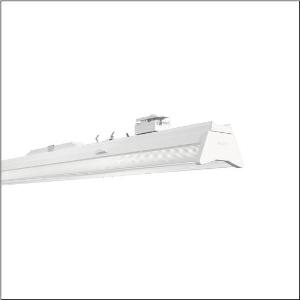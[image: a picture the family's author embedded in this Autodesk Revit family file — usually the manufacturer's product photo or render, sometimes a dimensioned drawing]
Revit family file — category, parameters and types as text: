
# Revit family: licross_r__21_performance_mo_52tm167n485g_c234
name_source: partatom
category: Lighting Fixtures
units: mm (PartAtom-declared; Revit-internal decimal feet)

## family parameters
Cut with Voids When Loaded = No
Host = Face
Light Source = No
Part Type = Normal
Room Calculation Point = No
Round Connector Dimension = Use Diameter
Shared = No

## types (1)
- Licross® 21 Performance MO (1 x LED, 8720 lm, 47.9 W, 4000K)
    Apparent Load = 48 VA
    CIE Flux Codes = 66 88 96 79 100
    Color Rendering = 80
    Color Temperature = 4000K
    Default Elevation = 1800 mm
    Description = Licross® 21 Performance MO, luminaire insert, of sheet steel, galvanised, coil coated, white, length: 1.500mm, width: 120mm, height: 123mm, LED rated luminous flux: 8.720lm, light colour: 840, SDCM (Standard Deviation of Colour Matching)MacAdam ≤ 3 SDCM (initial), control gear: ON/OFF, with plug, 3-pole, with phase selection, mains connection: 220..240V, AC, 50/60Hz, rated input power: 48W, internal wiring halogen-free, primary light control with lens, of plastic, primary optical cover: cover, of PMMA, light emission: direct/indirect distribution, primary light characteristic: symmetric, protection rating (complete): IP40, insulation class (complete): insulation class I (protective earthing), certification: CE, ENEC, UKCA, protection symbol: D if used in an environment without relevant dust loads with corresponding accessories, impact resistance: IK06, permissible ambient temperature for indoor applications: -35..+45°C, corresponds to IFS (International Featured Standards) requirements for safety and quality in the food industry, reducing of maximum allowable ambient temperature of 5°C with ceiling mounting, LABS conformity tested according to VDMA 24364:2018-05, packaging unit: 1 piece
    Height = 114 mm
    Lamp = 1 x LED
    Lamp Light Flux = 8720 lm
    Lamp Power = 47.9 W
    Lamp count = 1
    Length = 1500 mm
    Luminous efficacy = 182 lm/W
    Manufacturer = Siteco
    ModVariant = No
    Model = 52TM167N485G
    Mounting Place = Ceiling
    Mounting Type = Pendant
    Number of Poles = 1
    OnlyDefault = Yes
    Power Factor = 1
    Product Name = Licross® 21 Performance MO
    Product group = luminaire insert | ceiling pendant
    ProductGroupID = 901
    Protection Class = Protection class I
    Protection Degree = IP 40
    RLX_Detail_Level = 1
    RLX_Emergency_Light_Flux = 0 lm
    RLX_Emergency_Type = 0
    RLX_Emergency_Type_DB = No
    RlxData = <blob elided: 30489 chars, md5=f3272045>
    Socket = socket
    Standby Power = 0 W
    System Light Flux = 8720 lm
    System Power = 48 W
    Type Comments = Product without accessories
    Type Image = l_1256138.jpg
    URL = http://relux.com
    VarID = ---
    Voltage = 0 V
    Weight = 0.00 kg
    Width = 120 mm

## geometry (parser evidence)
native form markers: Blend x4, Sweep x13
no freeform markers — native parametric forms only
